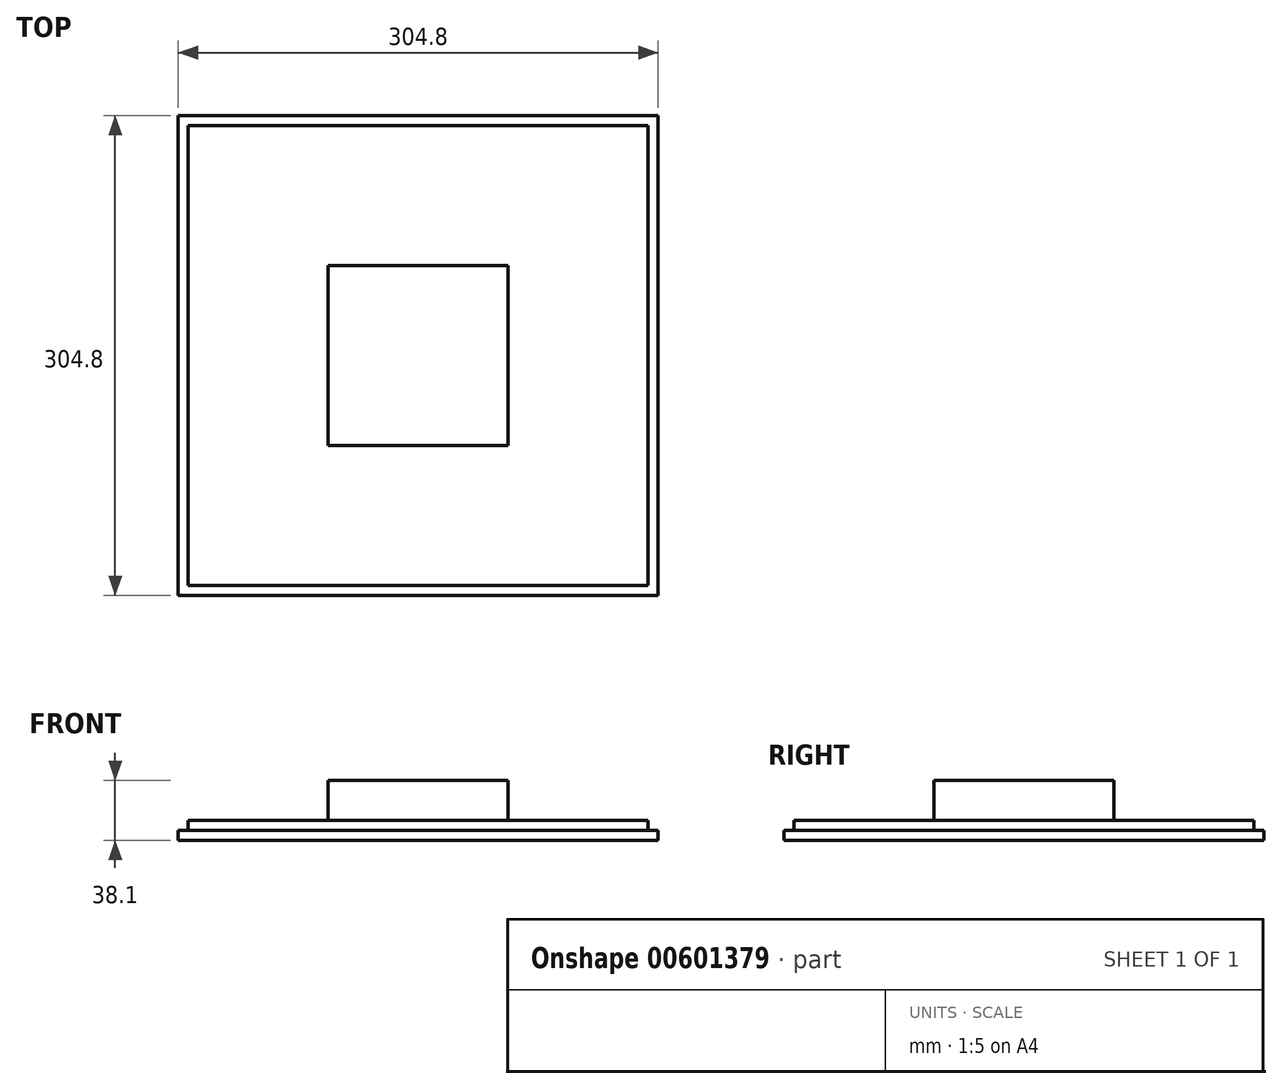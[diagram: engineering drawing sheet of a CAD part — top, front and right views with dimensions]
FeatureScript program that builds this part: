
annotation { "Feature Type Name" : "Feature", "Feature Type Description" : "" }
export const myFeature = defineFeature(function(context is Context, id is Id, definition is map)
    precondition{}
    {
        {
            var Q0;
            Q0=qCreatedBy(makeId("Top.planeOp"),FACE);
            var sketch = newSketch(context, id + "F0", { "sketchPlane" : qUnion([Q0])});
            skLineSegment(sketch, "E0.bottom", {"start": v(-152.4, 152.4) * mm, "end": v(152.4, 152.4) * mm});
            skLineSegment(sketch, "E0.top", {"start": v(-152.4, -152.4) * mm, "end": v(152.4, -152.4) * mm});
            skLineSegment(sketch, "E0.left", {"start": v(-152.4, 152.4) * mm, "end": v(-152.4, -152.4) * mm});
            skLineSegment(sketch, "E0.right", {"start": v(152.4, 152.4) * mm, "end": v(152.4, -152.4) * mm});
            skPoint(sketch, "E1.positionSnap0", {"position": v(152.4, 0) * mm});
            skPoint(sketch, "E2", {"position": v(0, 152.4) * mm});
            skLineSegment(sketch, "E3.bottom", {"start": v(-146.05, 146.05) * mm, "end": v(146.05, 146.05) * mm});
            skLineSegment(sketch, "E3.top", {"start": v(-146.05, -146.05) * mm, "end": v(146.05, -146.05) * mm});
            skLineSegment(sketch, "E3.left", {"start": v(-146.05, 146.05) * mm, "end": v(-146.05, -146.05) * mm});
            skLineSegment(sketch, "E3.right", {"start": v(146.05, 146.05) * mm, "end": v(146.05, -146.05) * mm});
            skPoint(sketch, "E4", {"position": v(0, 146.05) * mm});
            skPoint(sketch, "E5", {"position": v(146.05, 0) * mm});
            skSolve(sketch);
        }
        {
            var Q0;
            Q0 = qSketchRegion(id + "F0", true);
            extrude(context, id + "F1", {"entities" : qUnion([Q0]), "depth" : 6.35 * mm, "offsetDistance" : 25.4 * mm});
        }
        {
            var Q0;
            Q0=makeQuery(id+"F0.imprint","IMPRINT",FACE,{"disambiguationData":[TD([[makeQuery(id+"F0.imprint","IMPRINT",EDGE,{"derivedFrom":sQuery(id+"F0.wireOp",EDGE,"E3.bottom")}),-1.0]])]});
            extrude(context, id + "F2", {"entities" : qUnion([Q0]), "operationType" : NewBodyOperationType.ADD, "depth" : 12.7 * mm, "offsetDistance" : 25.4 * mm});
        }
        {
            var Q0;
            Q0=makeQuery(id+"F2.opExtrude","CAP_FACE",FACE,{"disambiguationData":[OSD([sQuery(id+"F0.wireOp",EDGE,"E3.bottom"),sQuery(id+"F0.wireOp",EDGE,"E3.top"),sQuery(id+"F0.wireOp",EDGE,"E3.left"),sQuery(id+"F0.wireOp",EDGE,"E3.right")])],"isStart":false});
            var sketch = newSketch(context, id + "F3", { "sketchPlane" : qUnion([Q0])});
            skLineSegment(sketch, "E6.bottom", {"start": v(-57.15, 57.15) * mm, "end": v(57.15, 57.15) * mm});
            skLineSegment(sketch, "E6.top", {"start": v(-57.15, -57.15) * mm, "end": v(57.15, -57.15) * mm});
            skLineSegment(sketch, "E6.left", {"start": v(-57.15, 57.15) * mm, "end": v(-57.15, -57.15) * mm});
            skLineSegment(sketch, "E6.right", {"start": v(57.15, 57.15) * mm, "end": v(57.15, -57.15) * mm});
            skPoint(sketch, "E7", {"position": v(0, 57.15) * mm});
            skPoint(sketch, "E8", {"position": v(-57.15, 0) * mm});
            skSolve(sketch);
        }
        {
            var Q0;
            Q0 = qSketchRegion(id + "F3", true);
            extrude(context, id + "F4", {"entities" : qUnion([Q0]), "operationType" : NewBodyOperationType.ADD, "depth" : 25.4 * mm, "offsetDistance" : 25.4 * mm});
        }
    });
